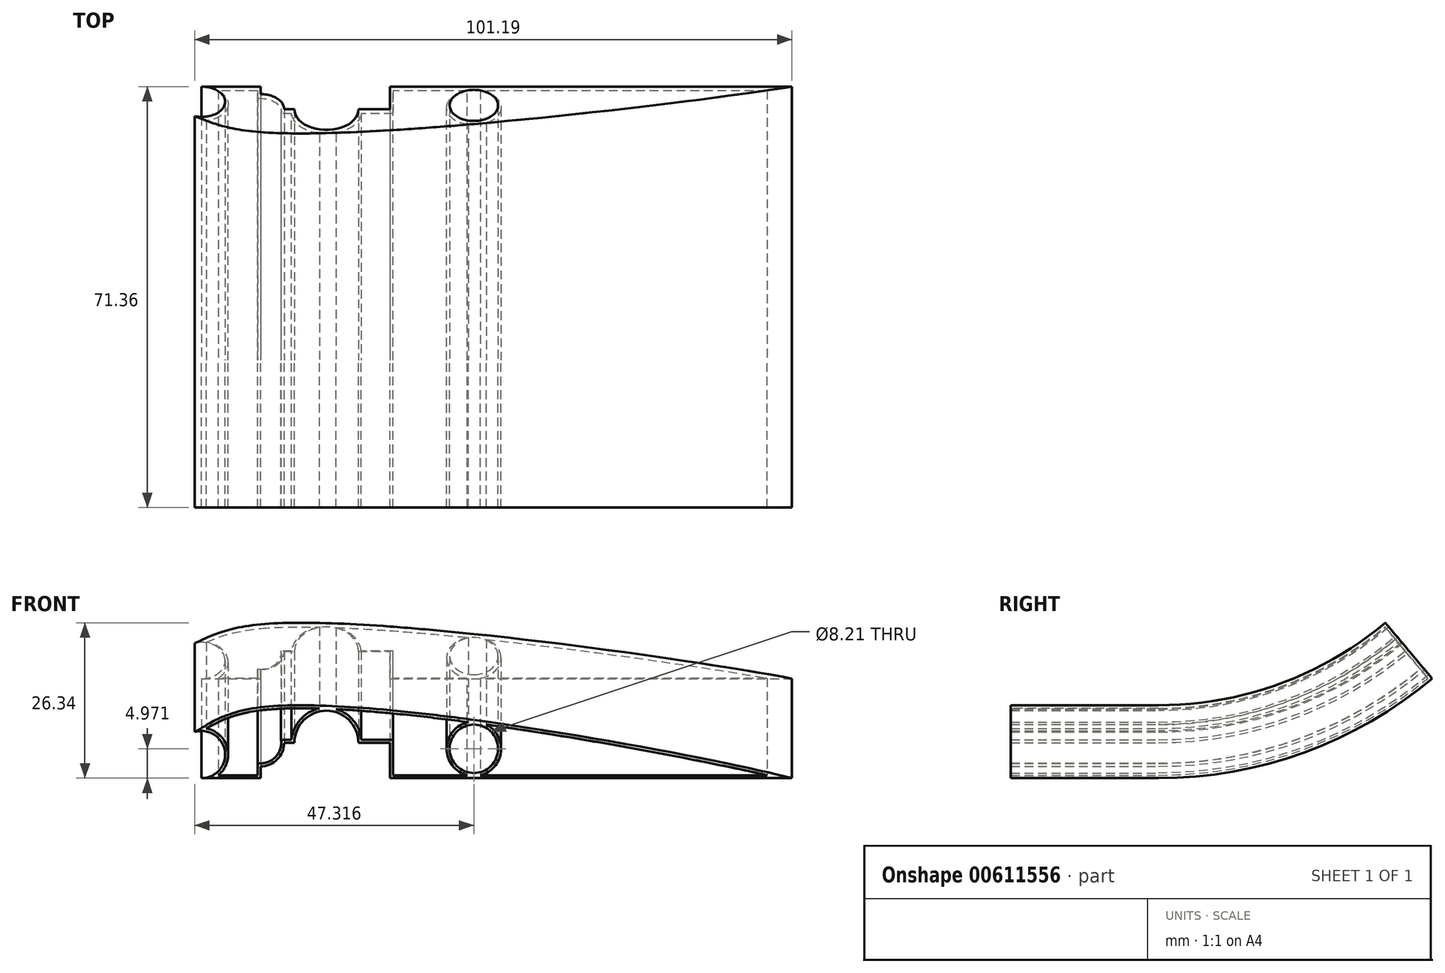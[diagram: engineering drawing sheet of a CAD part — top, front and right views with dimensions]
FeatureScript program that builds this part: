
annotation { "Feature Type Name" : "Feature", "Feature Type Description" : "" }
export const myFeature = defineFeature(function(context is Context, id is Id, definition is map)
    precondition{}
    {
        {
            var Q0;
            Q0=qCreatedBy(makeId("Front.planeOp"),FACE);
            var sketch = newSketch(context, id + "F0", { "sketchPlane" : qUnion([Q0])});
            skLineSegment(sketch, "E0", {"start": v(8.9, -4) * mm, "end": v(18.9, -4) * mm});
            skLineSegment(sketch, "E1", {"start": v(18.9, -4) * mm, "end": v(44.5, -4) * mm});
            skLineSegment(sketch, "E2", {"start": v(8.9, -4) * mm, "end": v(8.9, 4) * mm});
            skLineSegment(sketch, "E3", {"start": v(18.9, -4) * mm, "end": v(18.9, 8) * mm});
            skLineSegment(sketch, "E4", {"start": v(8.9, -4) * mm, "end": v(8.9, 0) * mm});
            skArc(sketch, "E5", {"start": v(8.9, -4) * mm, "mid": v(5.04, -1.04) * mm, "end": v(6.9, 3.46) * mm});
            skFitSpline(sketch, "E6", {"points": [v(6.9, 3.46) * mm, v(18.9, 8) * mm, v(108.9, -4) * mm], "startDerivative": vector(25.72, 9) * mm, "endDerivative": vector(55.93, -14.48) * mm});
            skLineSegment(sketch, "E7", {"start": v(44.5, -4) * mm, "end": v(108.9, -4) * mm});
            skLineSegment(sketch, "E8", {"start": v(44.5, -4) * mm, "end": v(40.83, -4) * mm});
            skLineSegment(sketch, "E9", {"start": v(40.83, -4) * mm, "end": v(40.83, 7.52) * mm});
            skCircle(sketch, "E10", {"center": v(8.9, 0) * mm, "radius": 4 * mm});
            skLineSegment(sketch, "E11", {"start": v(18.9, -4) * mm, "end": v(18.9, 2) * mm});
            skCircle(sketch, "E12", {"center": v(18.9, 2) * mm, "radius": 4 * mm});
            skLineSegment(sketch, "E13.right", {"start": v(55.04, 10.81) * mm, "end": v(55.04, -6.12) * mm});
            skLineSegment(sketch, "E14", {"start": v(18.9, 2) * mm, "end": v(30.05, 2) * mm});
            skLineSegment(sketch, "E15", {"start": v(30.05, 2) * mm, "end": v(40.83, 2) * mm});
            skLineSegment(sketch, "E16", {"start": v(40.83, 2) * mm, "end": v(55.04, 0.97) * mm});
            skCircle(sketch, "E17", {"center": v(30.05, 2) * mm, "radius": 5.42 * mm});
            skCircle(sketch, "E18", {"center": v(55.04, 0.97) * mm, "radius": 4.1 * mm});
            skLineSegment(sketch, "E19", {"start": v(8.9, 0) * mm, "end": v(8.9, 16.72) * mm});
            skLineSegment(sketch, "E20", {"start": v(8.9, 16.72) * mm, "end": v(40.51, 16.72) * mm});
            skLineSegment(sketch, "E21", {"start": v(8.9, 16.72) * mm, "end": v(8.9, 30.94) * mm});
            skLineSegment(sketch, "E22", {"start": v(8.9, 30.94) * mm, "end": v(43.34, 30.94) * mm});
            skLineSegment(sketch, "E23", {"start": v(8.9, 30.94) * mm, "end": v(8.9, 68.12) * mm});
            skPoint(sketch, "E23.endSnap0", {"position": v(8.9, 23.83) * mm});
            skLineSegment(sketch, "E24", {"start": v(8.9, 68.12) * mm, "end": v(29.87, 68.12) * mm});
            skSolve(sketch);
        }
        {
            var Q0;
            {var subQ1=sQuery(id+"F0.wireOp",EDGE,"E6");var subQ5=sQuery(id+"F0.wireOp",EDGE,"E9");var subQ6=makeQuery(id+"F0.imprint","INTERSECT",VERTEX,{"derivedFrom":[subQ1,subQ5]});Q0=makeQuery(id+"F0.imprint","IMPRINT",FACE,{"disambiguationData":[TD([[makeQuery(id+"F0.imprint","IMPRINT",EDGE,{"disambiguationData":[TD([[subQ6,-1.0]])],"derivedFrom":subQ1}),-1.0]])]});}
            var Q1;
            {var subQ1=sQuery(id+"F0.wireOp",EDGE,"E8");Q1=makeQuery(id+"F0.imprint","IMPRINT",FACE,{"disambiguationData":[TD([[makeQuery(id+"F0.imprint","IMPRINT",EDGE,{"derivedFrom":subQ1}),-1.0]])]});}
            var Q2;
            {var subQ1=sQuery(id+"F0.wireOp",EDGE,"E1");Q2=makeQuery(id+"F0.imprint","IMPRINT",FACE,{"disambiguationData":[TD([[makeQuery(id+"F0.imprint","IMPRINT",EDGE,{"derivedFrom":subQ1}),1.0]])]});}
            var Q3;
            {var subQ1=sQuery(id+"F0.wireOp",EDGE,"E3");var subQ10=sQuery(id+"F0.wireOp",EDGE,"E6");var subQ12=makeQuery(id+"F0.imprint","INTERSECT",VERTEX,{"derivedFrom":[subQ1,subQ10]});Q3=makeQuery(id+"F0.imprint","IMPRINT",FACE,{"disambiguationData":[TD([[makeQuery(id+"F0.imprint","IMPRINT",EDGE,{"disambiguationData":[TD([[subQ12,1.0]])],"derivedFrom":subQ1}),-1.0]])]});}
            var Q4;
            {var subQ1=sQuery(id+"F0.wireOp",EDGE,"E0");Q4=makeQuery(id+"F0.imprint","IMPRINT",FACE,{"disambiguationData":[TD([[makeQuery(id+"F0.imprint","IMPRINT",EDGE,{"derivedFrom":subQ1}),1.0]])]});}
            var Q5;
            {var subQ0=sQuery(id+"F0.wireOp",EDGE,"E4");Q5=makeQuery(id+"F0.imprint","IMPRINT",FACE,{"disambiguationData":[TD([[makeQuery(id+"F0.imprint","IMPRINT",EDGE,{"derivedFrom":subQ0}),-1.0]])]});}
            var Q6;
            {var subQ1=sQuery(id+"F0.wireOp",EDGE,"E4");Q6=makeQuery(id+"F0.imprint","IMPRINT",FACE,{"disambiguationData":[TD([[makeQuery(id+"F0.imprint","IMPRINT",EDGE,{"derivedFrom":subQ1}),1.0]])]});}
            var Q7;
            {var subQ1=sQuery(id+"F0.wireOp",EDGE,"E7");var subQ5=sQuery(id+"F0.wireOp",EDGE,"E6");var subQ6=makeQuery(id+"F0.imprint","INTERSECT",VERTEX,{"derivedFrom":[subQ5,subQ1]});Q7=makeQuery(id+"F0.imprint","IMPRINT",FACE,{"disambiguationData":[TD([[makeQuery(id+"F0.imprint","IMPRINT",EDGE,{"disambiguationData":[TD([[subQ6,1.0]])],"derivedFrom":subQ5}),-1.0]])]});}
            var Q8;
            {var subQ0=sQuery(id+"F0.wireOp",EDGE,"E19");var subQ1=sQuery(id+"F0.wireOp",EDGE,"E6");var subQ2=makeQuery(id+"F0.imprint","INTERSECT",VERTEX,{"derivedFrom":[subQ1,subQ0]});Q8=makeQuery(id+"F0.imprint","IMPRINT",FACE,{"disambiguationData":[TD([[makeQuery(id+"F0.imprint","IMPRINT",EDGE,{"disambiguationData":[TD([[subQ2,1.0]])],"derivedFrom":subQ1}),-1.0]])]});}
            var Q9;
            {var subQ1=sQuery(id+"F0.wireOp",EDGE,"E3");var subQ3=sQuery(id+"F0.wireOp",EDGE,"E12");var subQ4=makeQuery(id+"F0.imprint","INTERSECT",VERTEX,{"derivedFrom":[subQ1,subQ3]});Q9=makeQuery(id+"F0.imprint","IMPRINT",FACE,{"disambiguationData":[TD([[makeQuery(id+"F0.imprint","IMPRINT",EDGE,{"disambiguationData":[TD([[subQ4,-1.0]])],"derivedFrom":subQ3}),1.0]])]});}
            var Q10;
            {var subQ1=sQuery(id+"F0.wireOp",EDGE,"E11");var subQ3=sQuery(id+"F0.wireOp",EDGE,"E12");var subQ4=makeQuery(id+"F0.imprint","INTERSECT",VERTEX,{"derivedFrom":[subQ1,subQ3]});Q10=makeQuery(id+"F0.imprint","IMPRINT",FACE,{"disambiguationData":[TD([[makeQuery(id+"F0.imprint","IMPRINT",EDGE,{"disambiguationData":[TD([[subQ4,-1.0]])],"derivedFrom":subQ3}),1.0]])]});}
            var Q11;
            {var subQ1=sQuery(id+"F0.wireOp",EDGE,"E3");var subQ3=sQuery(id+"F0.wireOp",EDGE,"E12");var subQ4=makeQuery(id+"F0.imprint","INTERSECT",VERTEX,{"derivedFrom":[subQ1,subQ3]});Q11=makeQuery(id+"F0.imprint","IMPRINT",FACE,{"disambiguationData":[TD([[makeQuery(id+"F0.imprint","IMPRINT",EDGE,{"disambiguationData":[TD([[subQ4,1.0]])],"derivedFrom":subQ3}),1.0]])]});}
            var Q12;
            Q12=sQuery(id+"F0.wireOp",EDGE,"E24");
            revolve(context, id + "F1", {"entities" : qUnion([Q0, Q1, Q2, Q3, Q4, Q5, Q6, Q7, Q8, Q9, Q10, Q11]), "axis" : qUnion([Q12]), "revolveType" : RevolveType.ONE_DIRECTION, "angle" : 40 * degree});
        }
        {
            var Q0;
            Q0=makeQuery(id+"F1.opRevolve","CAP_FACE",FACE,{"disambiguationData":[OSD([sQuery(id+"F0.wireOp",EDGE,"E0"),sQuery(id+"F0.wireOp",EDGE,"E1"),sQuery(id+"F0.wireOp",EDGE,"E6"),sQuery(id+"F0.wireOp",EDGE,"E7"),sQuery(id+"F0.wireOp",EDGE,"E8"),sQuery(id+"F0.wireOp",EDGE,"E10"),sQuery(id+"F0.wireOp",EDGE,"E12"),sQuery(id+"F0.wireOp",EDGE,"E17"),sQuery(id+"F0.wireOp",EDGE,"E18")])],"isStart":true});
            extrude(context, id + "F2", {"entities" : qUnion([Q0]), "operationType" : NewBodyOperationType.ADD, "depth" : 25 * mm, "offsetDistance" : 25 * mm});
        }
        {
            var Q0;
            Q0=makeQuery(id+"F2.opExtrude","CAP_FACE",FACE,{"disambiguationData":[OSD([sQuery(id+"F0.wireOp",EDGE,"E0"),sQuery(id+"F0.wireOp",EDGE,"E1"),sQuery(id+"F0.wireOp",EDGE,"E6"),sQuery(id+"F0.wireOp",EDGE,"E7"),sQuery(id+"F0.wireOp",EDGE,"E8"),sQuery(id+"F0.wireOp",EDGE,"E10"),sQuery(id+"F0.wireOp",EDGE,"E12"),sQuery(id+"F0.wireOp",EDGE,"E17"),sQuery(id+"F0.wireOp",EDGE,"E18")])],"isStart":false});
            shell(context, id + "F3", {"entities" : qUnion([Q0]), "thickness" : 0.5 * mm});
        }
    });
